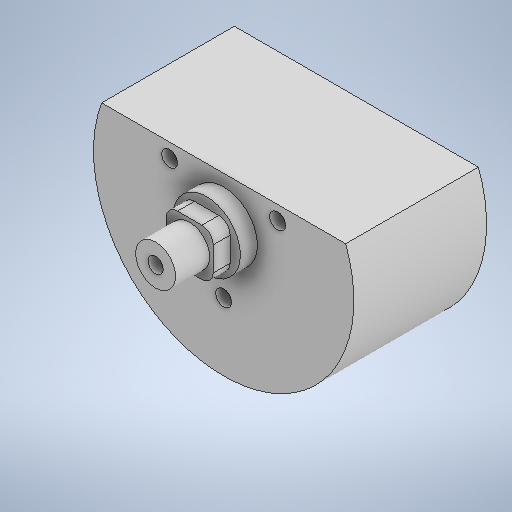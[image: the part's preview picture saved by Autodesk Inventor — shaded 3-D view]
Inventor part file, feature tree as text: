
AUTODESK INVENTOR PART (.ipt)
format: ipt  version: 2025.1 (Build 291241000, 241)  size: 294,912 bytes
history: native  units: mm
features: sketch x7, extrude x6, fillet x1, shell x1, projected_geometry x1
ambient origin geometry x8: Origin, YZ Plane, XZ Plane, XY Plane, X Axis, Y Axis, Z Axis, Center Point
bodies: Solid1 (feature_tree)
feature tree (16):
  extrude  "Extrusion1"  Depth=8.0mm
  extrude  "Extrusion2"  Depth=23.4mm
  extrude  "Extrusion3"  Depth=8.3mm
  fillet  "Fillet1"  Radius=8.3mm
  extrude  "Extrusion4"  Depth=2.0mm
  extrude  "Extrusion5"  Depth=6.0mm TaperAngle=0.0deg
  extrude  "Extrusion6"  Depth=10.0mm TaperAngle=0.0deg
  shell  "Shell1"  Thickness=2.8mm
  sketch  "Sketch1"  dims[d0=45.9mm d1=8.0mm]
  sketch  "Sketch2"  dims[d5=3.0mm d6=0.0mm d7=8.3mm d8=8.3mm]
  sketch  "Sketch3"  dims[d9=3.0mm d10=0.0mm d11=2.0mm]
  sketch  "Sketch4"  dims[d12=7.05mm d13=6.0mm d14=0.0mm]
  sketch  "Sketch5"  dims[d15=2.7mm d16=10.0mm d17=0.0mm d18=2.8mm]
  sketch  "Sketch6"  dims[d19=11.0mm d20=30.0mm d22=360.0deg d24=10.0mm d25=0.0mm d26=1.6mm]
  projected_geometry  "Projected Loop1"
  sketch  "Sketch Circular Pattern1"  dims[d2=23.4mm d3=0.0mm d4=11.9mm]
